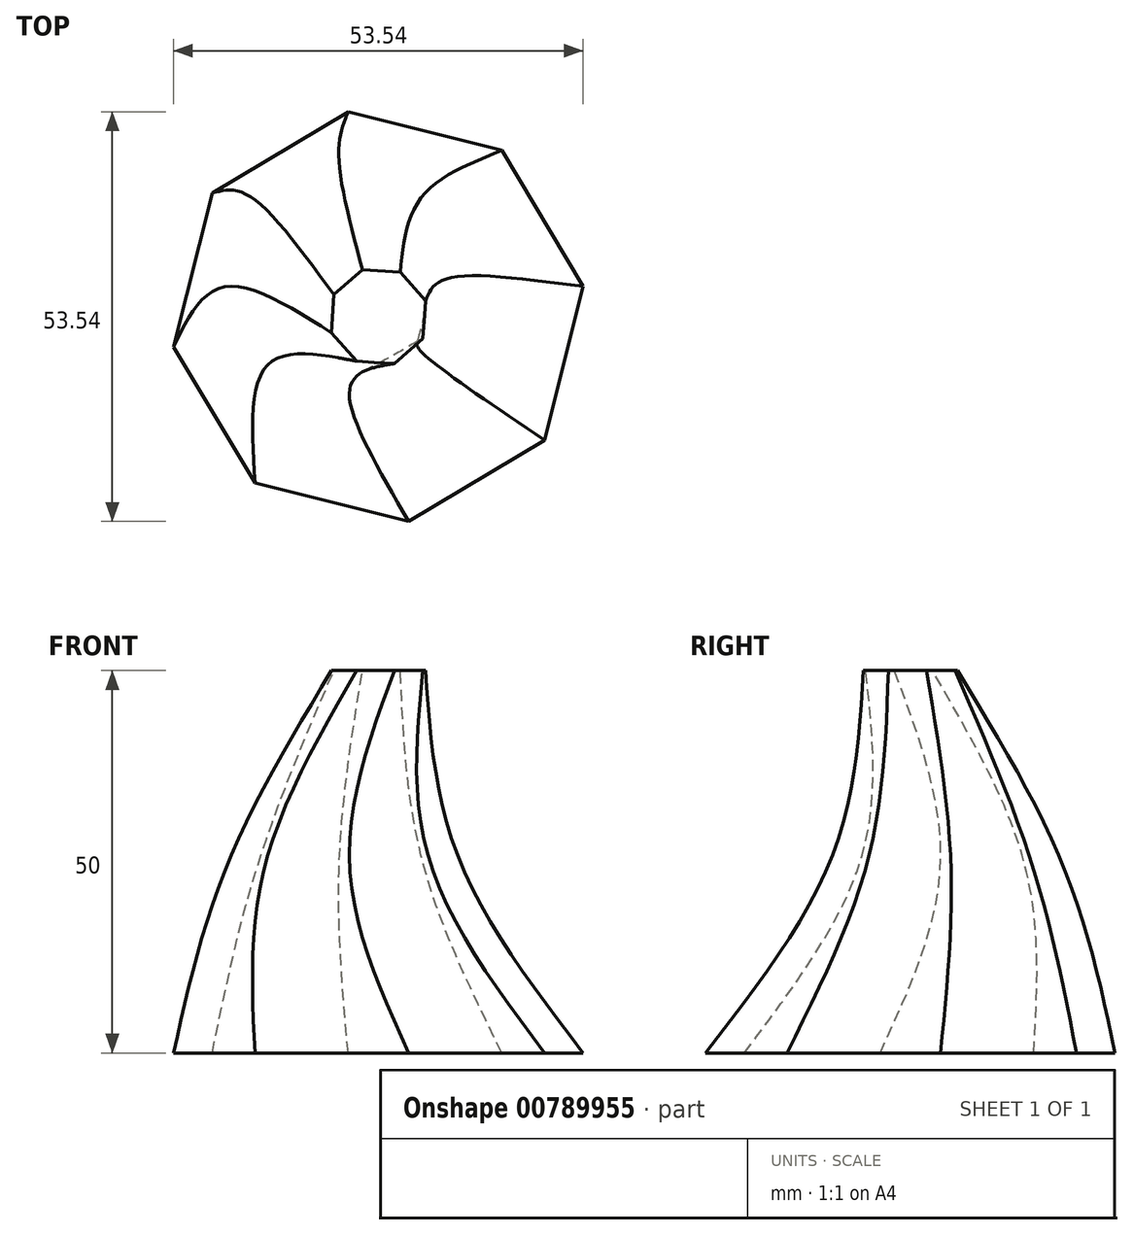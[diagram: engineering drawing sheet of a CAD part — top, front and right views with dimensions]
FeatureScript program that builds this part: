
annotation { "Feature Type Name" : "Feature", "Feature Type Description" : "" }
export const myFeature = defineFeature(function(context is Context, id is Id, definition is map)
    precondition{}
    {
        {
            var Q0;
            Q0=qCreatedBy(makeId("Top.planeOp"),FACE);
            var sketch = newSketch(context, id + "F0", { "sketchPlane" : qUnion([Q0])});
            skCircle(sketch, "E0.cCircle", {"center": v(0, 0) * mm, "radius": 25 * mm, "construction": true});
            skLineSegment(sketch, "E0.0", {"start": v(-21.72, 16.14) * mm, "end": v(-3.95, 26.77) * mm});
            skLineSegment(sketch, "E0.1", {"start": v(-3.95, 26.77) * mm, "end": v(16.14, 21.72) * mm});
            skLineSegment(sketch, "E0.2", {"start": v(16.14, 21.72) * mm, "end": v(26.77, 3.95) * mm});
            skLineSegment(sketch, "E0.3", {"start": v(26.77, 3.95) * mm, "end": v(21.72, -16.14) * mm});
            skLineSegment(sketch, "E0.4", {"start": v(21.72, -16.14) * mm, "end": v(3.95, -26.77) * mm});
            skLineSegment(sketch, "E0.5", {"start": v(3.95, -26.77) * mm, "end": v(-16.14, -21.72) * mm});
            skLineSegment(sketch, "E0.6", {"start": v(-16.14, -21.72) * mm, "end": v(-26.77, -3.95) * mm});
            skLineSegment(sketch, "E0.7", {"start": v(-26.77, -3.95) * mm, "end": v(-21.72, 16.14) * mm});
            skPoint(sketch, "E0.0.midPoint", {"position": v(-12.83, 21.45) * mm});
            skSolve(sketch);
        }
        {
            var Q0;
            Q0=qCreatedBy(makeId("Top.planeOp"),FACE);
            cPlane(context, id + "F1", {"entities" : qUnion([Q0]), "cplaneType" : CPlaneType.OFFSET, "offset" : 25 * mm, "width" : 150 * mm, "height" : 150 * mm});
        }
        {
            var Q0;
            Q0=qCreatedBy(id+"F1.planeOp",FACE);
            var sketch = newSketch(context, id + "F2", { "sketchPlane" : qUnion([Q0])});
            skCircle(sketch, "E1.cCircle", {"center": v(-4.45, 4.63) * mm, "radius": 14 * mm, "construction": true});
            skLineSegment(sketch, "E1.0", {"start": v(-15.62, 14.86) * mm, "end": v(-5.1, 19.77) * mm});
            skLineSegment(sketch, "E1.1", {"start": v(-5.1, 19.77) * mm, "end": v(5.8, 15.8) * mm});
            skLineSegment(sketch, "E1.2", {"start": v(5.8, 15.8) * mm, "end": v(10.7, 5.29) * mm});
            skLineSegment(sketch, "E1.3", {"start": v(10.7, 5.29) * mm, "end": v(6.73, -5.61) * mm});
            skLineSegment(sketch, "E1.4", {"start": v(6.73, -5.61) * mm, "end": v(-3.79, -10.51) * mm});
            skLineSegment(sketch, "E1.5", {"start": v(-3.79, -10.51) * mm, "end": v(-14.68, -6.54) * mm});
            skLineSegment(sketch, "E1.6", {"start": v(-14.68, -6.54) * mm, "end": v(-19.59, 3.97) * mm});
            skLineSegment(sketch, "E1.7", {"start": v(-19.59, 3.97) * mm, "end": v(-15.62, 14.86) * mm});
            skPoint(sketch, "E1.0.midPoint", {"position": v(-10.36, 17.32) * mm});
            skSolve(sketch);
        }
        {
            var Q0;
            Q0=qCreatedBy(makeId("Top.planeOp"),FACE);
            cPlane(context, id + "F3", {"entities" : qUnion([Q0]), "cplaneType" : CPlaneType.OFFSET, "offset" : 50 * mm, "width" : 150 * mm, "height" : 150 * mm});
        }
        {
            var Q0;
            Q0=qCreatedBy(id+"F3.planeOp",FACE);
            var sketch = newSketch(context, id + "F4", { "sketchPlane" : qUnion([Q0])});
            skCircle(sketch, "E2.cCircle", {"center": v(0, 0) * mm, "radius": 6 * mm, "construction": true});
            skLineSegment(sketch, "E2.0", {"start": v(-2.87, -5.83) * mm, "end": v(-6.15, -2.1) * mm});
            skLineSegment(sketch, "E2.1", {"start": v(-6.15, -2.1) * mm, "end": v(-5.83, 2.87) * mm});
            skLineSegment(sketch, "E2.2", {"start": v(-5.83, 2.87) * mm, "end": v(-2.1, 6.15) * mm});
            skLineSegment(sketch, "E2.3", {"start": v(-2.1, 6.15) * mm, "end": v(2.87, 5.83) * mm});
            skLineSegment(sketch, "E2.4", {"start": v(2.87, 5.83) * mm, "end": v(6.15, 2.1) * mm});
            skLineSegment(sketch, "E2.5", {"start": v(6.15, 2.1) * mm, "end": v(5.83, -2.87) * mm});
            skLineSegment(sketch, "E2.6", {"start": v(5.83, -2.87) * mm, "end": v(2.1, -6.15) * mm});
            skLineSegment(sketch, "E2.7", {"start": v(2.1, -6.15) * mm, "end": v(-2.87, -5.83) * mm});
            skPoint(sketch, "E2.0.midPoint", {"position": v(-4.5, -3.96) * mm});
            skSolve(sketch);
        }
        {
            var Q0;
            Q0 = qSketchRegion(id + "F0", true);
            var Q1;
            Q1 = qSketchRegion(id + "F2", true);
            var Q2;
            Q2 = qSketchRegion(id + "F4", true);
            loft(context, id + "F5", {"sheetProfilesArray" : [{ "sheetProfileEntities" : qUnion([Q0]) }, { "sheetProfileEntities" : qUnion([Q1]) }, { "sheetProfileEntities" : qUnion([Q2]) }]});
        }
    });
